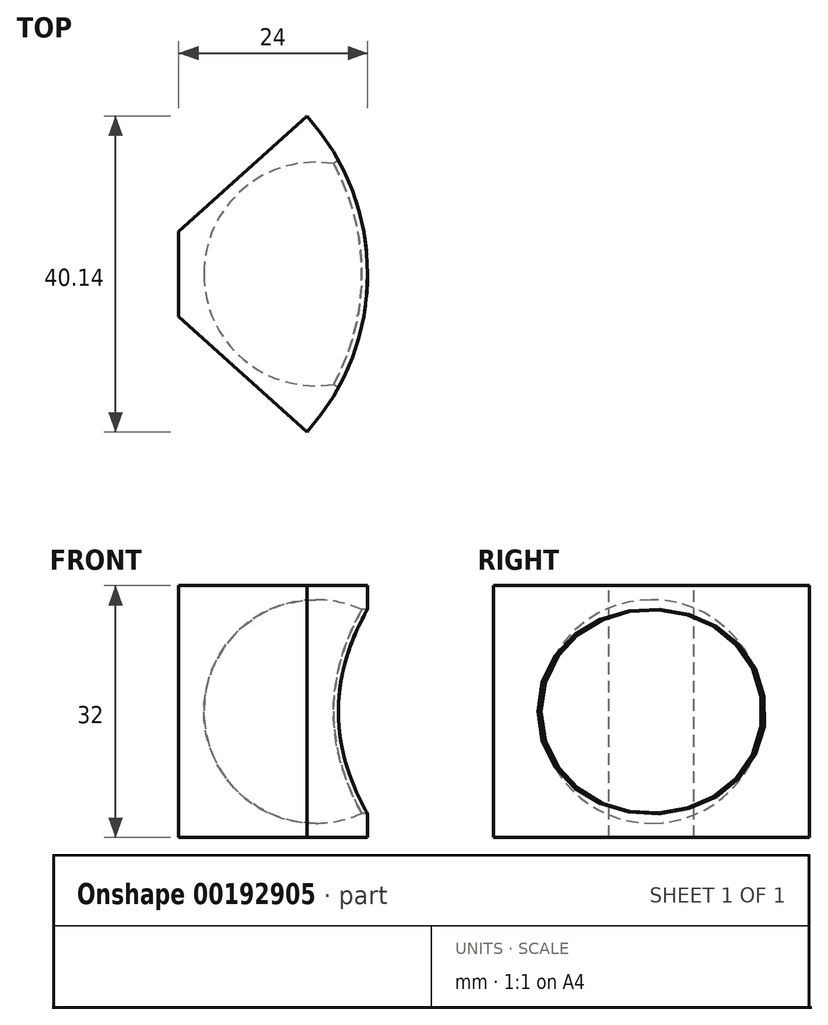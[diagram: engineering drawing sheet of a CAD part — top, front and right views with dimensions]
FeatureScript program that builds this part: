
annotation { "Feature Type Name" : "Feature", "Feature Type Description" : "" }
export const myFeature = defineFeature(function(context is Context, id is Id, definition is map)
    precondition{}
    {
        {
            var Q0;
            Q0=qCreatedBy(makeId("Top.planeOp"),FACE);
            var sketch = newSketch(context, id + "F0", { "sketchPlane" : qUnion([Q0])});
            skCircle(sketch, "E0", {"center": v(0, 0) * mm, "radius": 30 * mm});
            skSolve(sketch);
        }
        {
            var Q0;
            Q0 = qSketchRegion(id + "F0", true);
            extrude(context, id + "F1", {"entities" : qUnion([Q0]), "depth" : 32 * mm});
        }
        {
            var Q0;
            Q0=qCreatedBy(makeId("Front.planeOp"),FACE);
            var sketch = newSketch(context, id + "F2", { "sketchPlane" : qUnion([Q0])});
            skLineSegment(sketch, "E1", {"start": v(-30, 0) * mm, "end": v(-30, 32) * mm});
            skLineSegment(sketch, "E2.0", {"start": v(-30, 32) * mm, "end": v(30, 32) * mm});
            skLineSegment(sketch, "E3", {"start": v(0, 32) * mm, "end": v(0, 0) * mm});
            skLineSegment(sketch, "E4", {"start": v(0, 16) * mm, "end": v(23.4, 16) * mm});
            skCircle(sketch, "E5", {"center": v(23.4, 16) * mm, "radius": 14.2 * mm});
            skLineSegment(sketch, "E6", {"start": v(23.4, 16) * mm, "end": v(23.4, 1.8) * mm});
            skLineSegment(sketch, "E7", {"start": v(23.4, 16) * mm, "end": v(23.4, 30.2) * mm});
            skSolve(sketch);
        }
        {
            var Q0;
            {var subQ0=sQuery(id+"F2.wireOp",EDGE,"E6");Q0=makeQuery(id+"F2.imprint","IMPRINT",FACE,{"disambiguationData":[TD([[makeQuery(id+"F2.imprint","IMPRINT",EDGE,{"derivedFrom":subQ0}),1.0]])]});}
            var Q1;
            Q1=sQuery(id+"F2.wireOp",EDGE,"E7");
            revolve(context, id + "F3", {"operationType" : NewBodyOperationType.REMOVE, "entities" : qUnion([Q0]), "axis" : qUnion([Q1]), "revolveType" : RevolveType.FULL, "oppositeDirection" : true});
        }
        {
            var Q0;
            Q0=makeQuery(id+"F1.opExtrude","CAP_FACE",FACE,{"disambiguationData":[OSD([sQuery(id+"F0.wireOp",EDGE,"E0")])],"isStart":false});
            var sketch = newSketch(context, id + "F4", { "sketchPlane" : qUnion([Q0])});
            skLineSegment(sketch, "E8", {"start": v(0, 0) * mm, "end": v(22.3, 20.07) * mm});
            skCircle(sketch, "E9.0.0", {"center": v(0, 0) * mm, "radius": 30 * mm});
            skLineSegment(sketch, "E10", {"start": v(0, 0) * mm, "end": v(22.3, -20.07) * mm});
            skLineSegment(sketch, "E11", {"start": v(6, 5.4) * mm, "end": v(6, -5.4) * mm});
            skSolve(sketch);
        }
        {
            var Q0;
            {var subQ1=sQuery(id+"F4.wireOp",EDGE,"E8");var subQ5=sQuery(id+"F4.wireOp",EDGE,"E10");var subQ6=makeQuery(id+"F4.imprint","INTERSECT",VERTEX,{"derivedFrom":[subQ1,subQ5]});Q0=makeQuery(id+"F4.imprint","IMPRINT",FACE,{"disambiguationData":[TD([[makeQuery(id+"F4.imprint","IMPRINT",EDGE,{"disambiguationData":[TD([[subQ6,-1.0]])],"derivedFrom":subQ1}),1.0]])]});}
            var Q1;
            {var subQ3=sQuery(id+"F4.wireOp",EDGE,"E11");Q1=makeQuery(id+"F4.imprint","IMPRINT",FACE,{"disambiguationData":[TD([[makeQuery(id+"F4.imprint","IMPRINT",EDGE,{"derivedFrom":subQ3}),-1.0]])]});}
            extrude(context, id + "F5", {"entities" : qUnion([Q0, Q1]), "operationType" : NewBodyOperationType.REMOVE, "oppositeDirection" : true, "depth" : 40 * mm});
        }
        {
            var Q0;
            Q0=makeQuery(id+"F3.boolean.opBoolean","INTERSECT",EDGE,{"derivedFrom":[makeQuery(id+"F1.opExtrude","SWEPT_FACE",FACE,{"disambiguationData":[OSD([sQuery(id+"F0.wireOp",EDGE,"E0")])]}),makeQuery(id+"F3.opRevolve","SWEPT_FACE",FACE,{"disambiguationData":[OSD([sQuery(id+"F2.wireOp",EDGE,"E5")])]})]});
            chamfer(context, id + "F6", {"entities" : qUnion([Q0]), "chamferType" : ChamferType.OFFSET_ANGLE, "width" : 1 * mm, "oppositeDirection" : false, "angle" : 46 * degree, "tangentPropagation" : true});
        }
    });
